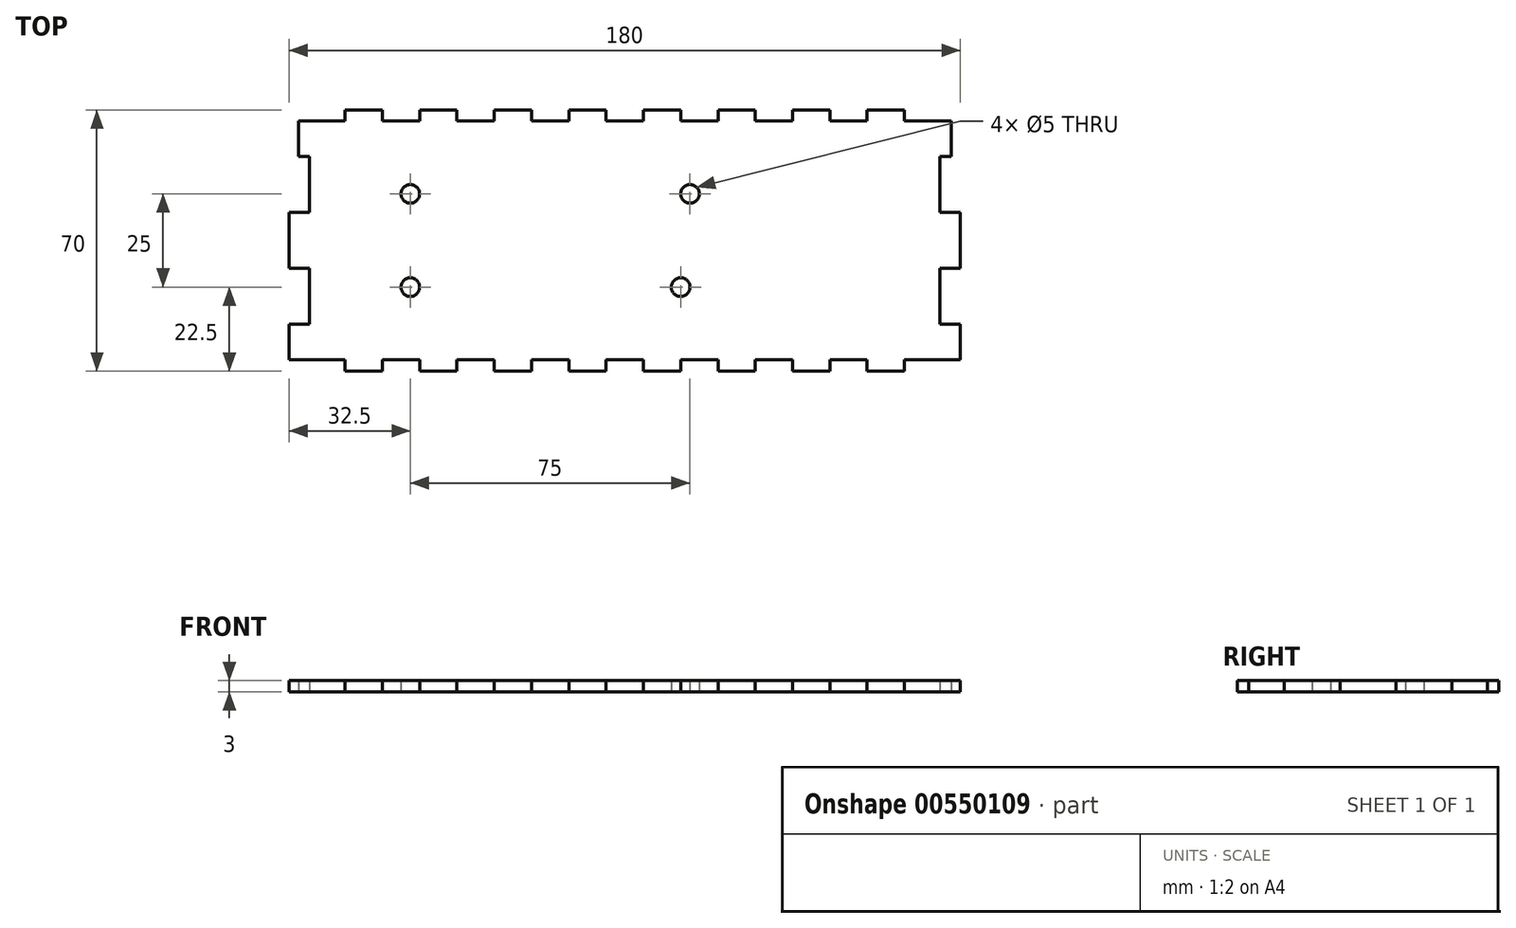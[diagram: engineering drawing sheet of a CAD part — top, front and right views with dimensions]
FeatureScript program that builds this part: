
annotation { "Feature Type Name" : "Feature", "Feature Type Description" : "" }
export const myFeature = defineFeature(function(context is Context, id is Id, definition is map)
    precondition{}
    {
        {
            var Q0;
            Q0=qCreatedBy(makeId("Top.planeOp"),FACE);
            var sketch = newSketch(context, id + "F0", { "sketchPlane" : qUnion([Q0])});
            skLineSegment(sketch, "E0", {"start": v(-49.5, 32) * mm, "end": v(-34.5, 32) * mm});
            skLineSegment(sketch, "E1", {"start": v(-34.5, 32) * mm, "end": v(-34.5, 35) * mm});
            skLineSegment(sketch, "E2", {"start": v(-34.5, 35) * mm, "end": v(-24.5, 35) * mm});
            skLineSegment(sketch, "E3", {"start": v(-24.5, 35) * mm, "end": v(-24.5, 32) * mm});
            skLineSegment(sketch, "E4", {"start": v(-24.5, 32) * mm, "end": v(-14.5, 32) * mm});
            skLineSegment(sketch, "E5", {"start": v(-14.5, 32) * mm, "end": v(-14.5, 35) * mm});
            skLineSegment(sketch, "E6", {"start": v(-14.5, 35) * mm, "end": v(-4.5, 35) * mm});
            skLineSegment(sketch, "E7", {"start": v(-4.5, 35) * mm, "end": v(-4.5, 32) * mm});
            skLineSegment(sketch, "E8", {"start": v(-4.5, 32) * mm, "end": v(5.5, 32) * mm});
            skLineSegment(sketch, "E9", {"start": v(5.5, 32) * mm, "end": v(5.5, 35) * mm});
            skLineSegment(sketch, "E10", {"start": v(5.5, 35) * mm, "end": v(15.5, 35) * mm});
            skLineSegment(sketch, "E11", {"start": v(15.5, 35) * mm, "end": v(15.5, 32) * mm});
            skLineSegment(sketch, "E12", {"start": v(15.5, 32) * mm, "end": v(25.5, 32) * mm});
            skLineSegment(sketch, "E13", {"start": v(25.5, 32) * mm, "end": v(25.5, 35) * mm});
            skLineSegment(sketch, "E14", {"start": v(25.5, 35) * mm, "end": v(35.5, 35) * mm});
            skLineSegment(sketch, "E15", {"start": v(35.5, 35) * mm, "end": v(35.5, 32) * mm});
            skLineSegment(sketch, "E16", {"start": v(35.5, -32) * mm, "end": v(35.5, -35) * mm});
            skLineSegment(sketch, "E17", {"start": v(35.5, -35) * mm, "end": v(25.5, -35) * mm});
            skLineSegment(sketch, "E18", {"start": v(25.5, -35) * mm, "end": v(25.5, -32) * mm});
            skLineSegment(sketch, "E19", {"start": v(25.5, -32) * mm, "end": v(15.5, -32) * mm});
            skLineSegment(sketch, "E20", {"start": v(15.5, -32) * mm, "end": v(15.5, -35) * mm});
            skLineSegment(sketch, "E21", {"start": v(15.5, -35) * mm, "end": v(5.5, -35) * mm});
            skLineSegment(sketch, "E22", {"start": v(5.5, -35) * mm, "end": v(5.5, -32) * mm});
            skLineSegment(sketch, "E23", {"start": v(5.5, -32) * mm, "end": v(-4.5, -32) * mm});
            skLineSegment(sketch, "E24", {"start": v(-4.5, -32) * mm, "end": v(-4.5, -35) * mm});
            skLineSegment(sketch, "E25", {"start": v(-4.5, -35) * mm, "end": v(-14.5, -35) * mm});
            skLineSegment(sketch, "E26", {"start": v(-14.5, -35) * mm, "end": v(-14.5, -32) * mm});
            skLineSegment(sketch, "E27", {"start": v(-14.5, -32) * mm, "end": v(-24.5, -32) * mm});
            skLineSegment(sketch, "E28", {"start": v(-24.5, -32) * mm, "end": v(-24.5, -35) * mm});
            skLineSegment(sketch, "E29", {"start": v(-24.5, -35) * mm, "end": v(-34.5, -35) * mm});
            skLineSegment(sketch, "E30", {"start": v(-34.5, -35) * mm, "end": v(-34.5, -32) * mm});
            skLineSegment(sketch, "E31", {"start": v(-34.5, -32) * mm, "end": v(-49.5, -32) * mm});
            skLineSegment(sketch, "E32", {"start": v(-47, 32) * mm, "end": v(-47, 22.5) * mm});
            skLineSegment(sketch, "E33", {"start": v(-47, 22.5) * mm, "end": v(-44, 22.5) * mm});
            skLineSegment(sketch, "E34", {"start": v(-44, 22.5) * mm, "end": v(-44, 7.5) * mm});
            skLineSegment(sketch, "E35", {"start": v(-44, 7.5) * mm, "end": v(-49.5, 7.5) * mm});
            skLineSegment(sketch, "E36", {"start": v(-49.5, 7.5) * mm, "end": v(-49.5, -7.5) * mm});
            skLineSegment(sketch, "E37", {"start": v(-49.5, -7.5) * mm, "end": v(-44, -7.5) * mm});
            skLineSegment(sketch, "E38", {"start": v(-44, -7.5) * mm, "end": v(-44, -22.5) * mm});
            skLineSegment(sketch, "E39", {"start": v(-44, -22.5) * mm, "end": v(-49.5, -22.5) * mm});
            skLineSegment(sketch, "E40", {"start": v(-49.5, -22.5) * mm, "end": v(-49.5, -32) * mm});
            skLineSegment(sketch, "E41", {"start": v(40.5, 58.2) * mm, "end": v(40.5, -58.58) * mm, "construction": true});
            skLineSegment(sketch, "E42", {"start": v(35.5, 32) * mm, "end": v(40.5, 32) * mm});
            skLineSegment(sketch, "E43", {"start": v(35.5, -32) * mm, "end": v(40.5, -32) * mm});
            skLineSegment(sketch, "E44.MirrorCS", {"start": v(75.5, 32) * mm, "end": v(75.5, 35) * mm});
            skLineSegment(sketch, "E45.MirrorCS", {"start": v(115.5, 32) * mm, "end": v(115.5, 35) * mm});
            skLineSegment(sketch, "E46.MirrorCS", {"start": v(75.5, -35) * mm, "end": v(75.5, -32) * mm});
            skLineSegment(sketch, "E47.MirrorCS", {"start": v(85.5, 35) * mm, "end": v(85.5, 32) * mm});
            skLineSegment(sketch, "E48.MirrorCS", {"start": v(105.5, 35) * mm, "end": v(105.5, 32) * mm});
            skLineSegment(sketch, "E49.MirrorCS", {"start": v(95.5, -35) * mm, "end": v(95.5, -32) * mm});
            skLineSegment(sketch, "E50.MirrorCS", {"start": v(95.5, 32) * mm, "end": v(95.5, 35) * mm});
            skLineSegment(sketch, "E51.MirrorCS", {"start": v(55.5, -35) * mm, "end": v(55.5, -32) * mm});
            skLineSegment(sketch, "E52.MirrorCS", {"start": v(45.5, -32) * mm, "end": v(45.5, -35) * mm});
            skLineSegment(sketch, "E53.MirrorCS", {"start": v(130.5, -7.5) * mm, "end": v(125, -7.5) * mm});
            skLineSegment(sketch, "E54.MirrorCS", {"start": v(128, 22.5) * mm, "end": v(125, 22.5) * mm});
            skLineSegment(sketch, "E55.MirrorCS", {"start": v(115.5, -35) * mm, "end": v(115.5, -32) * mm});
            skLineSegment(sketch, "E56.MirrorCS", {"start": v(85.5, -32) * mm, "end": v(85.5, -35) * mm});
            skLineSegment(sketch, "E57.MirrorCS", {"start": v(125, -22.5) * mm, "end": v(130.5, -22.5) * mm});
            skLineSegment(sketch, "E58.MirrorCS", {"start": v(65.5, 35) * mm, "end": v(65.5, 32) * mm});
            skLineSegment(sketch, "E59.MirrorCS", {"start": v(45.5, 35) * mm, "end": v(45.5, 32) * mm});
            skLineSegment(sketch, "E60.MirrorCS", {"start": v(65.5, -32) * mm, "end": v(65.5, -35) * mm});
            skLineSegment(sketch, "E61.MirrorCS", {"start": v(55.5, 32) * mm, "end": v(55.5, 35) * mm});
            skLineSegment(sketch, "E62.MirrorCS", {"start": v(105.5, -32) * mm, "end": v(105.5, -35) * mm});
            skLineSegment(sketch, "E63.MirrorCS", {"start": v(125, 7.5) * mm, "end": v(130.5, 7.5) * mm});
            skLineSegment(sketch, "E64.MirrorCS", {"start": v(65.5, -35) * mm, "end": v(75.5, -35) * mm});
            skLineSegment(sketch, "E65.MirrorCS", {"start": v(115.5, 35) * mm, "end": v(105.5, 35) * mm});
            skLineSegment(sketch, "E66.MirrorCS", {"start": v(95.5, -32) * mm, "end": v(105.5, -32) * mm});
            skLineSegment(sketch, "E67.MirrorCS", {"start": v(75.5, -32) * mm, "end": v(85.5, -32) * mm});
            skLineSegment(sketch, "E68.MirrorCS", {"start": v(130.5, 32) * mm, "end": v(115.5, 32) * mm});
            skLineSegment(sketch, "E69.MirrorCS", {"start": v(55.5, 35) * mm, "end": v(45.5, 35) * mm});
            skLineSegment(sketch, "E70.MirrorCS", {"start": v(125, 22.5) * mm, "end": v(125, 7.5) * mm});
            skLineSegment(sketch, "E71.MirrorCS", {"start": v(55.5, -32) * mm, "end": v(65.5, -32) * mm});
            skLineSegment(sketch, "E72.MirrorCS", {"start": v(45.5, 32) * mm, "end": v(40.5, 32) * mm});
            skLineSegment(sketch, "E73.MirrorCS", {"start": v(128, 32) * mm, "end": v(128, 22.5) * mm});
            skLineSegment(sketch, "E74.MirrorCS", {"start": v(130.5, 7.5) * mm, "end": v(130.5, -7.5) * mm});
            skLineSegment(sketch, "E75.MirrorCS", {"start": v(45.5, -32) * mm, "end": v(40.5, -32) * mm});
            skLineSegment(sketch, "E76.MirrorCS", {"start": v(75.5, 35) * mm, "end": v(65.5, 35) * mm});
            skLineSegment(sketch, "E77.MirrorCS", {"start": v(105.5, -35) * mm, "end": v(115.5, -35) * mm});
            skLineSegment(sketch, "E78.MirrorCS", {"start": v(115.5, -32) * mm, "end": v(130.5, -32) * mm});
            skLineSegment(sketch, "E79.MirrorCS", {"start": v(65.5, 32) * mm, "end": v(55.5, 32) * mm});
            skLineSegment(sketch, "E80.MirrorCS", {"start": v(95.5, 35) * mm, "end": v(85.5, 35) * mm});
            skLineSegment(sketch, "E81.MirrorCS", {"start": v(130.5, -22.5) * mm, "end": v(130.5, -32) * mm});
            skLineSegment(sketch, "E82.MirrorCS", {"start": v(105.5, 32) * mm, "end": v(95.5, 32) * mm});
            skLineSegment(sketch, "E83.MirrorCS", {"start": v(85.5, 32) * mm, "end": v(75.5, 32) * mm});
            skLineSegment(sketch, "E84.MirrorCS", {"start": v(85.5, -35) * mm, "end": v(95.5, -35) * mm});
            skLineSegment(sketch, "E85.MirrorCS", {"start": v(45.5, -35) * mm, "end": v(55.5, -35) * mm});
            skLineSegment(sketch, "E86.MirrorCS", {"start": v(125, -7.5) * mm, "end": v(125, -22.5) * mm});
            skCircle(sketch, "E87", {"center": v(58, 12.5) * mm, "radius": 2.5 * mm});
            skCircle(sketch, "E88", {"center": v(55.5, -12.5) * mm, "radius": 2.5 * mm});
            skCircle(sketch, "E89", {"center": v(-17, 12.5) * mm, "radius": 2.5 * mm});
            skCircle(sketch, "E90", {"center": v(-17, -12.5) * mm, "radius": 2.5 * mm});
            skSolve(sketch);
        }
        {
            var Q0;
            Q0=makeQuery(id+"F0.imprint","IMPRINT",FACE,{"disambiguationData":[TD([[makeQuery(id+"F0.imprint","IMPRINT",EDGE,{"derivedFrom":sQuery(id+"F0.wireOp",EDGE,"E0")}),-1.0]])]});
            extrude(context, id + "F1", {"entities" : qUnion([Q0]), "depth" : 3 * mm, "offsetDistance" : 25 * mm});
        }
    });
